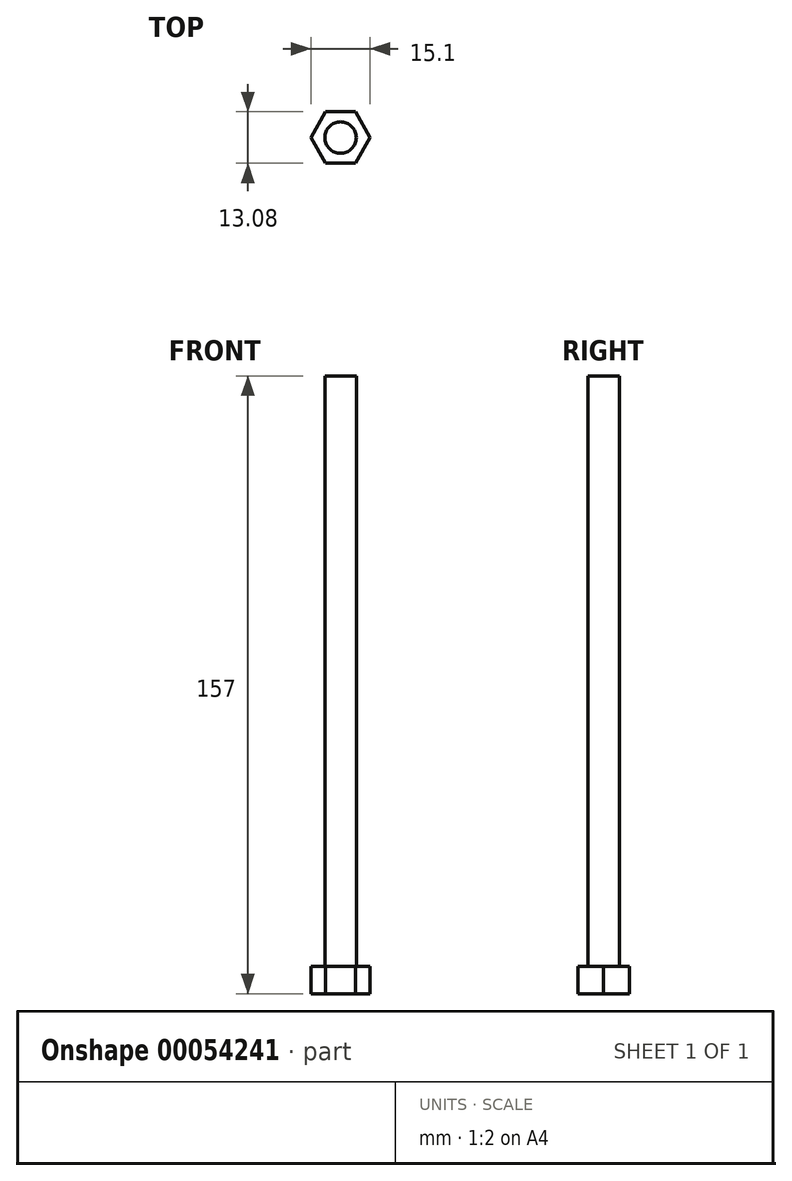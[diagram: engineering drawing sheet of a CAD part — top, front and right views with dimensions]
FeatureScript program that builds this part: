
annotation { "Feature Type Name" : "Feature", "Feature Type Description" : "" }
export const myFeature = defineFeature(function(context is Context, id is Id, definition is map)
    precondition{}
    {
        {
            var Q0;
            Q0=qCreatedBy(makeId("Top.planeOp"),FACE);
            var sketch = newSketch(context, id + "F0", { "sketchPlane" : qUnion([Q0])});
            skCircle(sketch, "E0.cCircle", {"center": v(0, 0) * mm, "radius": 7.55 * mm, "construction": true});
            skLineSegment(sketch, "E0.0", {"start": v(3.77, -6.54) * mm, "end": v(-3.77, -6.54) * mm});
            skLineSegment(sketch, "E0.1", {"start": v(-3.77, -6.54) * mm, "end": v(-7.55, 0) * mm});
            skLineSegment(sketch, "E0.2", {"start": v(-7.55, 0) * mm, "end": v(-3.77, 6.54) * mm});
            skLineSegment(sketch, "E0.3", {"start": v(-3.77, 6.54) * mm, "end": v(3.77, 6.54) * mm});
            skLineSegment(sketch, "E0.4", {"start": v(3.77, 6.54) * mm, "end": v(7.55, 0) * mm});
            skLineSegment(sketch, "E0.5", {"start": v(7.55, 0) * mm, "end": v(3.77, -6.54) * mm});
            skSolve(sketch);
        }
        {
            var Q0;
            Q0 = qSketchRegion(id + "F0", true);
            extrude(context, id + "F1", {"entities" : qUnion([Q0]), "depth" : 7 * mm});
        }
        {
            var Q0;
            Q0=makeQuery(id+"F1.opExtrude","CAP_FACE",FACE,{"disambiguationData":[OSD([sQuery(id+"F0.wireOp",EDGE,"E0.0"),sQuery(id+"F0.wireOp",EDGE,"E0.1"),sQuery(id+"F0.wireOp",EDGE,"E0.2"),sQuery(id+"F0.wireOp",EDGE,"E0.3"),sQuery(id+"F0.wireOp",EDGE,"E0.4"),sQuery(id+"F0.wireOp",EDGE,"E0.5")])],"isStart":false});
            var sketch = newSketch(context, id + "F2", { "sketchPlane" : qUnion([Q0])});
            skCircle(sketch, "E1", {"center": v(0, 0) * mm, "radius": 4 * mm});
            skSolve(sketch);
        }
        {
            var Q0;
            Q0 = qSketchRegion(id + "F2", true);
            extrude(context, id + "F3", {"entities" : qUnion([Q0]), "operationType" : NewBodyOperationType.ADD, "depth" : 150 * mm});
        }
    });
